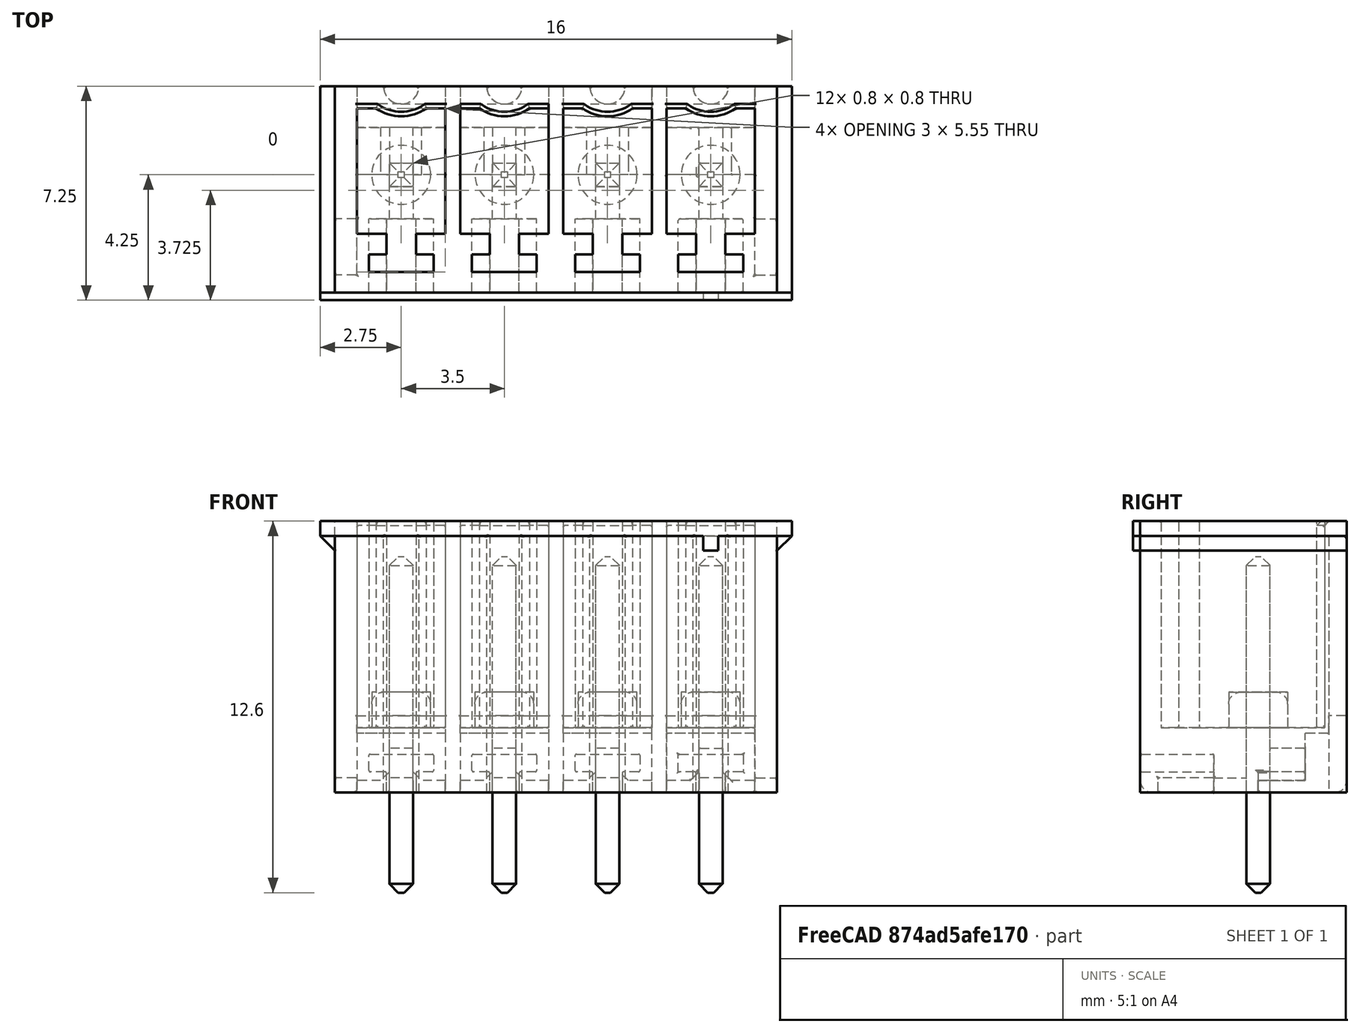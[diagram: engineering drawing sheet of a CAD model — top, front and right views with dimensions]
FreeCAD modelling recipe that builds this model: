
FCSTD DOCUMENT  (FreeCAD 0.15R4671 (Git))
Label: 4PIN
License: All rights reserved
LicenseURL: http://en.wikipedia.org/wiki/All_rights_reserved
objects: PartDesign::Fillet×102, PartDesign::Chamfer×18, Sketcher::SketchObject×15, PartDesign::Pocket×9, PartDesign::LinearPattern×9, PartDesign::Pad×6, PartDesign::Mirrored×2, Image::ImagePlane×1, Part::Cut×1
note: 177 computed .brp shape members not serialized (recipe doc carries the construction recipe); baked Part::Feature solids carry a one-line shape summary decoded from their .brp

FEATURE [Sketcher::SketchObject] Sketch
  sketch-geometry (4):
    g0: LineSegment StartX=-7.5 StartY=3 StartZ=0 EndX=7.5 EndY=3 EndZ=0
    g1: LineSegment StartX=7.5 StartY=3 StartZ=0 EndX=7.5 EndY=-4 EndZ=0
    g2: LineSegment StartX=7.5 StartY=-4 StartZ=0 EndX=-7.5 EndY=-4 EndZ=0
    g3: LineSegment StartX=-7.5 StartY=-4 StartZ=0 EndX=-7.5 EndY=3 EndZ=0
  constraints (12):
    c: Coincident(g0,g1)
    c: Coincident(g1,g2)
    c: Coincident(g2,g3)
    c: Coincident(g3,g0)
    c: Horizontal(g0)
    c: Horizontal(g2)
    c: Vertical(g1)
    c: Vertical(g3)
    c: DistanceX(g0) = 15
    c: DistanceY(g1) = -7
    c: Symmetric(g0,g0,g-2)
    c: DistanceY(g-1,g2) = -4
FEATURE [PartDesign::Pad] Pad
  Length = 9.2
  Length2 = 100
  Sketch = -> Sketch
  Type = 0
FEATURE [Sketcher::SketchObject] Sketch001
  Placement = pos=(0,0,-3.4) rot=(0,0,1;0rad)
  sketch-geometry (16):
    g0: LineSegment StartX=-5.65 StartY=0.4 StartZ=0 EndX=-4.85 EndY=0.4 EndZ=0
    g1: LineSegment StartX=-4.85 StartY=0.4 StartZ=0 EndX=-4.85 EndY=-0.4 EndZ=0
    g2: LineSegment StartX=-4.85 StartY=-0.4 StartZ=0 EndX=-5.65 EndY=-0.4 EndZ=0
    g3: LineSegment StartX=-5.65 StartY=-0.4 StartZ=0 EndX=-5.65 EndY=0.4 EndZ=0
    g4: LineSegment StartX=-2.15 StartY=0.4 StartZ=0 EndX=-1.35 EndY=0.4 EndZ=0
    g5: LineSegment StartX=-1.35 StartY=0.4 StartZ=0 EndX=-1.35 EndY=-0.4 EndZ=0
    g6: LineSegment StartX=-1.35 StartY=-0.4 StartZ=0 EndX=-2.15 EndY=-0.4 EndZ=0
    g7: LineSegment StartX=-2.15 StartY=-0.4 StartZ=0 EndX=-2.15 EndY=0.4 EndZ=0
    g8: LineSegment StartX=1.35 StartY=0.4 StartZ=0 EndX=2.15 EndY=0.4 EndZ=0
    g9: LineSegment StartX=2.15 StartY=0.4 StartZ=0 EndX=2.15 EndY=-0.4 EndZ=0
    g10: LineSegment StartX=2.15 StartY=-0.4 StartZ=0 EndX=1.35 EndY=-0.4 EndZ=0
    g11: LineSegment StartX=1.35 StartY=-0.4 StartZ=0 EndX=1.35 EndY=0.4 EndZ=0
    g12: LineSegment StartX=4.85 StartY=0.4 StartZ=0 EndX=5.65 EndY=0.4 EndZ=0
    g13: LineSegment StartX=5.65 StartY=0.4 StartZ=0 EndX=5.65 EndY=-0.4 EndZ=0
    g14: LineSegment StartX=5.65 StartY=-0.4 StartZ=0 EndX=4.85 EndY=-0.4 EndZ=0
    g15: LineSegment StartX=4.85 StartY=-0.4 StartZ=0 EndX=4.85 EndY=0.4 EndZ=0
  constraints (48):
    c: Coincident(g0,g1)
    c: Coincident(g1,g2)
    c: Coincident(g2,g3)
    c: Coincident(g3,g0)
    c: Horizontal(g0)
    c: Horizontal(g2)
    c: Vertical(g1)
    c: Vertical(g3)
    c: Coincident(g4,g5)
    c: Coincident(g5,g6)
    c: Coincident(g6,g7)
    c: Coincident(g7,g4)
    c: Horizontal(g4)
    c: Horizontal(g6)
    c: Vertical(g5)
    c: Vertical(g7)
    c: Coincident(g8,g9)
    c: Coincident(g9,g10)
    c: Coincident(g10,g11)
    c: Coincident(g11,g8)
    c: Horizontal(g8)
    c: Horizontal(g10)
    c: Vertical(g9)
    c: Vertical(g11)
    c: Coincident(g12,g13)
    c: Coincident(g13,g14)
    c: Coincident(g14,g15)
    c: Coincident(g15,g12)
    c: Horizontal(g12)
    c: Horizontal(g14)
    c: Vertical(g13)
    c: Vertical(g15)
    c: Equal(g0,g1)
    c: Equal(g1,g4)
    c: Equal(g4,g5)
    c: Equal(g5,g8)
    c: Equal(g8,g9)
    c: Equal(g9,g12)
    c: Equal(g12,g13)
    c: DistanceX(g0) = 0.8
    c: Symmetric(g1,g0,g-1)
    c: Symmetric(g4,g5,g-1)
    c: Symmetric(g8,g10,g-1)
    c: Symmetric(g12,g14,g-1)
    c: Symmetric(g4,g8,g-2)
    c: DistanceX(g-1,g5) = -1.35
    c: DistanceX(g5,g1) = -3.5
    c: DistanceX(g10,g14) = 3.5
FEATURE [PartDesign::Pad] Pad001
  Length = 11.4
  Length2 = 100
  Placement = pos=(0,0,-3.4) rot=(0,0,1;0rad)
  Sketch = -> Sketch001
  Type = 0
FEATURE [Sketcher::SketchObject] Sketch002
  Placement = pos=(0,0,9.2) rot=(0,0,1;0rad)
  Support = -> Pad [Face6]
  sketch-geometry (14):
    g0: LineSegment StartX=-6.1 StartY=2.25 StartZ=0 EndX=-6.75 EndY=2.25 EndZ=0
    g1: LineSegment StartX=-6.75 StartY=2.25 StartZ=0 EndX=-6.75 EndY=-2 EndZ=0
    g2: LineSegment StartX=-6.75 StartY=-2 StartZ=0 EndX=-5.75 EndY=-2 EndZ=0
    g3: LineSegment StartX=-5.75 StartY=-2 StartZ=0 EndX=-5.75 EndY=-2.7 EndZ=0
    g4: LineSegment StartX=-5.75 StartY=-2.7 StartZ=0 EndX=-6.35 EndY=-2.7 EndZ=0
    g5: LineSegment StartX=-6.35 StartY=-2.7 StartZ=0 EndX=-6.35 EndY=-3.3 EndZ=0
    g6: LineSegment StartX=-6.35 StartY=-3.3 StartZ=0 EndX=-4.15 EndY=-3.3 EndZ=0
    g7: LineSegment StartX=-4.15 StartY=-3.3 StartZ=0 EndX=-4.15 EndY=-2.7 EndZ=0
    g8: LineSegment StartX=-4.15 StartY=-2.7 StartZ=0 EndX=-4.75 EndY=-2.7 EndZ=0
    g9: LineSegment StartX=-4.75 StartY=-2.7 StartZ=0 EndX=-4.75 EndY=-2 EndZ=0
    g10: LineSegment StartX=-4.75 StartY=-2 StartZ=0 EndX=-3.75 EndY=-2 EndZ=0
    g11: LineSegment StartX=-3.75 StartY=-2 StartZ=0 EndX=-3.75 EndY=2.25 EndZ=0
    g12: LineSegment StartX=-3.75 StartY=2.25 StartZ=0 EndX=-4.4 EndY=2.25 EndZ=0
    g13: ArcOfCircle CenterX=-5.25 CenterY=3.48592 CenterZ=0 NormalX=0 NormalY=0 NormalZ=1 Radius=1.5 StartAngle=4.10993 EndAngle=5.31484
  constraints (43):
    c: Horizontal(g0)
    c: Coincident(g0,g1)
    c: Vertical(g1)
    c: Coincident(g1,g2)
    c: Horizontal(g2)
    c: Coincident(g2,g3)
    c: Vertical(g3)
    c: Coincident(g3,g4)
    c: Horizontal(g4)
    c: Coincident(g4,g5)
    c: Vertical(g5)
    c: Coincident(g5,g6)
    c: Horizontal(g6)
    c: Coincident(g6,g7)
    c: Vertical(g7)
    c: Coincident(g7,g8)
    c: Horizontal(g8)
    c: Coincident(g8,g9)
    c: Vertical(g9)
    c: Coincident(g9,g10)
    c: Horizontal(g10)
    c: Coincident(g10,g11)
    c: Vertical(g11)
    c: Coincident(g11,g12)
    c: Horizontal(g12)
    c: Equal(g1,g11)
    c: Equal(g0,g12)
    c: Equal(g2,g10)
    c: Equal(g3,g9)
    c: Equal(g4,g8)
    c: Equal(g5,g7)
    c: DistanceY(g1) = -4.25
    c: DistanceY(g3) = -0.7
    c: DistanceY(g7) = 0.6
    c: DistanceY(g-1,g9) = -2
    c: Coincident(g13,g0)
    c: Coincident(g13,g12)
    c: Radius(g13) = 1.5
    c: DistanceX(g0,g11) = 3
    c: DistanceX(g0) = -0.65
    c: DistanceX(g3,g8) = 1
    c: DistanceX(g6) = 2.2
    c: DistanceX(g-1,g13) = -5.25
FEATURE [Image::ImagePlane] ImagePlane
  Placement = pos=(0,-0.6,9.2) rot=(0,0,1;0rad)
  XSize = 11.5
  YSize = 7.25
FEATURE [PartDesign::Pocket] Pocket
  Length = 7
  Sketch = -> Sketch002
  Type = 0
FEATURE [PartDesign::LinearPattern] LinearPattern
  Direction = -> Sketch002 [H_Axis]
  Length = 10.5
  Occurrences = 4
  Originals = -> [Pocket]
FEATURE [Sketcher::SketchObject] Sketch003
  Placement = pos=(0,0,2.2) rot=(0,0,1;0rad)
  Support = -> LinearPattern [Face65]
  sketch-geometry (1):
    g0: Circle CenterX=-5.25 CenterY=0 CenterZ=0 NormalX=0 NormalY=0 NormalZ=1 Radius=1
  constraints (3):
    c: PointOnObject(g0,g-1)
    c: Radius(g0) = 1
    c: DistanceX(g-1,g0) = -5.25
FEATURE [PartDesign::Pad] Pad002
  Length = 1.2
  Length2 = 100
  Sketch = -> Sketch003
  Type = 0
FEATURE [PartDesign::LinearPattern] LinearPattern001
  Direction = -> Sketch003 [H_Axis]
  Length = 10.5
  Occurrences = 4
  Originals = -> [Pad002]
FEATURE [Sketcher::SketchObject] Sketch004
  Placement = pos=(0,0,-3.4) rot=(0,0,1;0rad)
  sketch-geometry (16):
    g0: LineSegment StartX=-5.65 StartY=0.4 StartZ=0 EndX=-4.85 EndY=0.4 EndZ=0
    g1: LineSegment StartX=-4.85 StartY=0.4 StartZ=0 EndX=-4.85 EndY=-0.4 EndZ=0
    g2: LineSegment StartX=-4.85 StartY=-0.4 StartZ=0 EndX=-5.65 EndY=-0.4 EndZ=0
    g3: LineSegment StartX=-5.65 StartY=-0.4 StartZ=0 EndX=-5.65 EndY=0.4 EndZ=0
    g4: LineSegment StartX=-2.15 StartY=0.4 StartZ=0 EndX=-1.35 EndY=0.4 EndZ=0
    g5: LineSegment StartX=-1.35 StartY=0.4 StartZ=0 EndX=-1.35 EndY=-0.4 EndZ=0
    g6: LineSegment StartX=-1.35 StartY=-0.4 StartZ=0 EndX=-2.15 EndY=-0.4 EndZ=0
    g7: LineSegment StartX=-2.15 StartY=-0.4 StartZ=0 EndX=-2.15 EndY=0.4 EndZ=0
    g8: LineSegment StartX=1.35 StartY=0.4 StartZ=0 EndX=2.15 EndY=0.4 EndZ=0
    g9: LineSegment StartX=2.15 StartY=0.4 StartZ=0 EndX=2.15 EndY=-0.4 EndZ=0
    g10: LineSegment StartX=2.15 StartY=-0.4 StartZ=0 EndX=1.35 EndY=-0.4 EndZ=0
    g11: LineSegment StartX=1.35 StartY=-0.4 StartZ=0 EndX=1.35 EndY=0.4 EndZ=0
    g12: LineSegment StartX=4.85 StartY=0.4 StartZ=0 EndX=5.65 EndY=0.4 EndZ=0
    g13: LineSegment StartX=5.65 StartY=0.4 StartZ=0 EndX=5.65 EndY=-0.4 EndZ=0
    g14: LineSegment StartX=5.65 StartY=-0.4 StartZ=0 EndX=4.85 EndY=-0.4 EndZ=0
    g15: LineSegment StartX=4.85 StartY=-0.4 StartZ=0 EndX=4.85 EndY=0.4 EndZ=0
  constraints (48):
    c: Coincident(g0,g1)
    c: Coincident(g1,g2)
    c: Coincident(g2,g3)
    c: Coincident(g3,g0)
    c: Horizontal(g0)
    c: Horizontal(g2)
    c: Vertical(g1)
    c: Vertical(g3)
    c: Coincident(g4,g5)
    c: Coincident(g5,g6)
    c: Coincident(g6,g7)
    c: Coincident(g7,g4)
    c: Horizontal(g4)
    c: Horizontal(g6)
    c: Vertical(g5)
    c: Vertical(g7)
    c: Coincident(g8,g9)
    c: Coincident(g9,g10)
    c: Coincident(g10,g11)
    c: Coincident(g11,g8)
    c: Horizontal(g8)
    c: Horizontal(g10)
    c: Vertical(g9)
    c: Vertical(g11)
    c: Coincident(g12,g13)
    c: Coincident(g13,g14)
    c: Coincident(g14,g15)
    c: Coincident(g15,g12)
    c: Horizontal(g12)
    c: Horizontal(g14)
    c: Vertical(g13)
    c: Vertical(g15)
    c: Equal(g0,g1)
    c: Equal(g1,g4)
    c: Equal(g4,g5)
    c: Equal(g5,g8)
    c: Equal(g8,g9)
    c: Equal(g9,g12)
    c: Equal(g12,g13)
    c: DistanceX(g0) = 0.8
    c: Symmetric(g1,g0,g-1)
    c: Symmetric(g4,g5,g-1)
    c: Symmetric(g8,g10,g-1)
    c: Symmetric(g12,g14,g-1)
    c: Symmetric(g4,g8,g-2)
    c: DistanceX(g-1,g5) = -1.35
    c: DistanceX(g5,g1) = -3.5
    c: DistanceX(g10,g14) = 3.5
FEATURE [PartDesign::Pad] Pad003
  Length = 10.2
  Length2 = 100
  Placement = pos=(0,0,-3.4) rot=(0,0,1;0rad)
  Sketch = -> Sketch004
  Type = 0
FEATURE [Part::Cut] Cut
  Base = -> LinearPattern001
  Tool = -> Pad003
FEATURE [Sketcher::SketchObject] Sketch005
  Placement = pos=(0,0,0) rot=(1,0,0;3.14159rad)
  Support = -> Cut [Face8]
  sketch-geometry (2):
    g0: LineSegment StartX=-5.85 StartY=-3 StartZ=0 EndX=-4.65 EndY=-3 EndZ=0
    g1: ArcOfCircle CenterX=-5.25 CenterY=-3 CenterZ=0 NormalX=0 NormalY=0 NormalZ=1 Radius=0.6 StartAngle=0 EndAngle=3.14159
  constraints (7):
    c: Horizontal(g0)
    c: DistanceX(g0) = 1.2
    c: PointOnObject(g1,g0)
    c: Coincident(g1,g0)
    c: Coincident(g1,g0)
    c: DistanceX(g-1,g1) = -5.25
    c: DistanceY(g-1,g1) = -3
FEATURE [PartDesign::Pocket] Pocket001
  Length = 8.7
  Sketch = -> Sketch005
  Type = 0
FEATURE [PartDesign::LinearPattern] LinearPattern002
  Direction = -> Sketch005 [H_Axis]
  Length = 10.5
  Occurrences = 4
  Originals = -> [Pocket001]
FEATURE [Sketcher::SketchObject] Sketch006
  ExternalGeometry = -> [LinearPattern002]
  Placement = pos=(0,-4,0) rot=(1,0,0;1.5708rad)
  Support = -> LinearPattern002 [Face29]
  sketch-geometry (4):
    g0: LineSegment StartX=-7.5 StartY=9.2 StartZ=0 EndX=-8 EndY=9.2 EndZ=0
    g1: LineSegment StartX=-8 StartY=9.2 StartZ=0 EndX=-8 EndY=8.7 EndZ=0
    g2: LineSegment StartX=-8 StartY=8.7 StartZ=0 EndX=-7.5 EndY=8.2 EndZ=0
    g3: LineSegment StartX=-7.5 StartY=8.2 StartZ=0 EndX=-7.5 EndY=9.2 EndZ=0
  constraints (11):
    c: Horizontal(g0)
    c: Coincident(g0,g1)
    c: Vertical(g1)
    c: Coincident(g1,g2)
    c: Coincident(g2,g3)
    c: Coincident(g3,g0)
    c: Vertical(g3)
    c: Coincident(g0,g-3)
    c: DistanceX(g0) = -0.5
    c: DistanceY(g1) = -0.5
    c: Angle(g-3,g2) = 0.785398
FEATURE [PartDesign::Pad] Pad004
  Length = 7
  Length2 = 100
  Reversed = true
  Sketch = -> Sketch006
  Type = 0
FEATURE [PartDesign::Mirrored] Mirrored
  MirrorPlane = -> Sketch006 [V_Axis]
  Originals = -> [Pad004]
FEATURE [Sketcher::SketchObject] Sketch007
  ExternalGeometry = -> [Mirrored]
  Placement = pos=(0,-4,0) rot=(1,0,0;1.5708rad)
  Support = -> Mirrored [Face101]
  sketch-geometry (8):
    g0: LineSegment StartX=-8 StartY=9.2 StartZ=0 EndX=8 EndY=9.2 EndZ=0
    g1: LineSegment StartX=8 StartY=9.2 StartZ=0 EndX=8 EndY=8.7 EndZ=0
    g2: LineSegment StartX=8 StartY=8.7 StartZ=0 EndX=5.5 EndY=8.7 EndZ=0
    g3: LineSegment StartX=-8 StartY=8.7 StartZ=0 EndX=-8 EndY=9.2 EndZ=0
    g4: LineSegment StartX=5 StartY=8.7 StartZ=0 EndX=5 EndY=8.2 EndZ=0
    g5: LineSegment StartX=5 StartY=8.2 StartZ=0 EndX=5.5 EndY=8.2 EndZ=0
    g6: LineSegment StartX=5.5 StartY=8.2 StartZ=0 EndX=5.5 EndY=8.7 EndZ=0
    g7: LineSegment StartX=5 StartY=8.7 StartZ=0 EndX=-8 EndY=8.7 EndZ=0
  constraints (25):
    c: Coincident(g0,g1)
    c: Coincident(g1,g2)
    c: Coincident(g7,g3)
    c: Coincident(g3,g0)
    c: Horizontal(g0)
    c: Horizontal(g2)
    c: Vertical(g1)
    c: Vertical(g3)
    c: PointOnObject(g0,g-3)
    c: DistanceY(g3) = 0.5
    c: PointOnObject(g0,g-4)
    c: Symmetric(g0,g0,g-2)
    c: Coincident(g4,g5)
    c: Coincident(g5,g6)
    c: Horizontal(g5)
    c: Vertical(g4)
    c: Vertical(g6)
    c: PointOnObject(g6,g2)
    c: DistanceY(g4,g-5) = 0
    c: Equal(g5,g4)
    c: DistanceX(g-1,g4) = 5
    c: PointOnObject(g2,g6)
    c: PointOnObject(g7,g4)
    c: Tangent(g2,g7)
    c: DistanceX(g2) = -2.5
FEATURE [PartDesign::Pad] Pad005
  Length = 0.25
  Length2 = 100
  Sketch = -> Sketch007
  Type = 0
FEATURE [Sketcher::SketchObject] Sketch008
  Placement = pos=(0,-4,0) rot=(1,0,0;1.5708rad)
  Support = -> Pad005 [Face66]
  sketch-geometry (8):
    g0: LineSegment StartX=-5.75 StartY=0 StartZ=0 EndX=-5.75 EndY=0.7 EndZ=0
    g1: LineSegment StartX=-5.75 StartY=0.7 StartZ=0 EndX=-6.35 EndY=0.7 EndZ=0
    g2: LineSegment StartX=-6.35 StartY=0.7 StartZ=0 EndX=-6.35 EndY=1.3 EndZ=0
    g3: LineSegment StartX=-6.35 StartY=1.3 StartZ=0 EndX=-4.15 EndY=1.3 EndZ=0
    g4: LineSegment StartX=-4.15 StartY=1.3 StartZ=0 EndX=-4.15 EndY=0.7 EndZ=0
    g5: LineSegment StartX=-4.15 StartY=0.7 StartZ=0 EndX=-4.75 EndY=0.7 EndZ=0
    g6: LineSegment StartX=-4.75 StartY=0.7 StartZ=0 EndX=-4.75 EndY=0 EndZ=0
    g7: LineSegment StartX=-4.75 StartY=0 StartZ=0 EndX=-5.75 EndY=0 EndZ=0
  constraints (25):
    c: Vertical(g0)
    c: Coincident(g0,g1)
    c: Horizontal(g1)
    c: Coincident(g1,g2)
    c: Coincident(g2,g3)
    c: Horizontal(g3)
    c: Coincident(g3,g4)
    c: Coincident(g4,g5)
    c: Horizontal(g5)
    c: Coincident(g5,g6)
    c: Vertical(g6)
    c: Coincident(g6,g7)
    c: Horizontal(g7)
    c: Coincident(g0,g7)
    c: Vertical(g4)
    c: Equal(g5,g1)
    c: Vertical(g2)
    c: Equal(g4,g2)
    c: Equal(g0,g6)
    c: DistanceX(g3) = 2.2
    c: DistanceX(g7) = -1
    c: DistanceY(g4) = -0.6
    c: DistanceY(g-1,g4) = 0.7
    c: DistanceX(g-1,g6) = -4.75
    c: PointOnObject(g6,g-1)
FEATURE [PartDesign::Pocket] Pocket002
  Length = 2.5
  Sketch = -> Sketch008
  Type = 0
FEATURE [PartDesign::LinearPattern] LinearPattern003
  Direction = -> Sketch008 [H_Axis]
  Length = 10.5
  Occurrences = 4
  Originals = -> [Pocket002]
FEATURE [Sketcher::SketchObject] Sketch009
  Placement = pos=(0,3,0) rot=(0,0.707107,0.707107;3.14159rad)
  Support = -> LinearPattern003 [Face10]
  sketch-geometry (4):
    g0: LineSegment StartX=-6.75 StartY=2 StartZ=0 EndX=-3.75 EndY=2 EndZ=0
    g1: LineSegment StartX=-3.75 StartY=2 StartZ=0 EndX=-3.75 EndY=0 EndZ=0
    g2: LineSegment StartX=-3.75 StartY=0 StartZ=0 EndX=-6.75 EndY=0 EndZ=0
    g3: LineSegment StartX=-6.75 StartY=0 StartZ=0 EndX=-6.75 EndY=2 EndZ=0
  constraints (12):
    c: Coincident(g0,g1)
    c: Coincident(g1,g2)
    c: Coincident(g2,g3)
    c: Coincident(g3,g0)
    c: Horizontal(g0)
    c: Horizontal(g2)
    c: Vertical(g1)
    c: Vertical(g3)
    c: PointOnObject(g1,g-1)
    c: DistanceX(g2) = -3
    c: DistanceY(g1) = -2
    c: DistanceX(g-1,g1) = -3.75
FEATURE [PartDesign::Pocket] Pocket003
  Length = 1.4
  Sketch = -> Sketch009
  Type = 0
FEATURE [PartDesign::LinearPattern] LinearPattern004
  Direction = -> Sketch009 [H_Axis]
  Length = 10.5
  Occurrences = 4
  Originals = -> [Pocket003]
FEATURE [Sketcher::SketchObject] Sketch010
  ExternalGeometry = -> [LinearPattern004]
  Placement = pos=(0,3,0) rot=(0,0.707107,0.707107;3.14159rad)
  Support = -> LinearPattern004 [Face10]
  sketch-geometry (4):
    g0: LineSegment StartX=-6.75 StartY=2 StartZ=0 EndX=-3.75 EndY=2 EndZ=0
    g1: LineSegment StartX=-3.75 StartY=2 StartZ=0 EndX=-3.75 EndY=2.6 EndZ=0
    g2: LineSegment StartX=-3.75 StartY=2.6 StartZ=0 EndX=-6.75 EndY=2.6 EndZ=0
    g3: LineSegment StartX=-6.75 StartY=2.6 StartZ=0 EndX=-6.75 EndY=2 EndZ=0
  constraints (11):
    c: Coincident(g0,g1)
    c: Coincident(g1,g2)
    c: Coincident(g2,g3)
    c: Coincident(g3,g0)
    c: Horizontal(g0)
    c: Horizontal(g2)
    c: Vertical(g1)
    c: Vertical(g3)
    c: Coincident(g0,g-3)
    c: DistanceX(g0) = 3
    c: DistanceY(g1) = 0.6
FEATURE [PartDesign::Pocket] Pocket004
  Length = 0.6
  Sketch = -> Sketch010
  Type = 0
FEATURE [PartDesign::LinearPattern] LinearPattern005
  Direction = -> Sketch010 [H_Axis]
  Length = 10.5
  Occurrences = 4
  Originals = -> [Pocket004]
FEATURE [Sketcher::SketchObject] Sketch011
  ExternalGeometry = -> [LinearPattern005]
  Placement = pos=(0,0,0) rot=(1,0,0;3.14159rad)
  Support = -> LinearPattern005 [Face72]
  sketch-geometry (4):
    g0: LineSegment StartX=-6.75 StartY=-1.6 StartZ=0 EndX=-3.75 EndY=-1.6 EndZ=0
    g1: LineSegment StartX=-3.75 StartY=-1.6 StartZ=0 EndX=-3.75 EndY=0 EndZ=0
    g2: LineSegment StartX=-3.75 StartY=0 StartZ=0 EndX=-6.75 EndY=0 EndZ=0
    g3: LineSegment StartX=-6.75 StartY=0 StartZ=0 EndX=-6.75 EndY=-1.6 EndZ=0
  constraints (11):
    c: Coincident(g0,g1)
    c: Coincident(g1,g2)
    c: Coincident(g2,g3)
    c: Coincident(g3,g0)
    c: Horizontal(g0)
    c: Horizontal(g2)
    c: Vertical(g1)
    c: Vertical(g3)
    c: Coincident(g0,g-4)
    c: PointOnObject(g1,g-1)
    c: Coincident(g0,g-4)
FEATURE [PartDesign::Pocket] Pocket005
  Length = 0.4
  Sketch = -> Sketch011
  Type = 0
FEATURE [PartDesign::LinearPattern] LinearPattern006
  Direction = -> Sketch011 [H_Axis]
  Length = 10.5
  Occurrences = 4
  Originals = -> [Pocket005]
FEATURE [Sketcher::SketchObject] Sketch012
  ExternalGeometry = -> [LinearPattern006]
  Placement = pos=(0,0,0) rot=(1,0,0;3.14159rad)
  Support = -> LinearPattern006 [Face72]
  sketch-geometry (4):
    g0: LineSegment StartX=-5.65 StartY=0.4 StartZ=0 EndX=-4.85 EndY=0.4 EndZ=0
    g1: LineSegment StartX=-4.85 StartY=0.4 StartZ=0 EndX=-4.85 EndY=1.5 EndZ=0
    g2: LineSegment StartX=-4.85 StartY=1.5 StartZ=0 EndX=-5.65 EndY=1.5 EndZ=0
    g3: LineSegment StartX=-5.65 StartY=1.5 StartZ=0 EndX=-5.65 EndY=0.4 EndZ=0
  constraints (11):
    c: Coincident(g0,g1)
    c: Coincident(g1,g2)
    c: Coincident(g2,g3)
    c: Coincident(g3,g0)
    c: Horizontal(g0)
    c: Horizontal(g2)
    c: Vertical(g1)
    c: Vertical(g3)
    c: Coincident(g0,g-4)
    c: PointOnObject(g2,g-5)
    c: Coincident(g0,g-3)
FEATURE [PartDesign::Pocket] Pocket006
  Length = 0.5
  Sketch = -> Sketch012
  Type = 0
FEATURE [PartDesign::LinearPattern] LinearPattern007
  Direction = -> Sketch012 [H_Axis]
  Length = 10.5
  Occurrences = 4
  Originals = -> [Pocket006]
FEATURE [Sketcher::SketchObject] Sketch013
  ExternalGeometry = -> [LinearPattern007]
  Placement = pos=(0,0,0.4) rot=(1,0,0;3.14159rad)
  Support = -> LinearPattern007 [Face114]
  sketch-geometry (4):
    g0: LineSegment StartX=-5.65 StartY=-0.4 StartZ=0 EndX=-4.85 EndY=-0.4 EndZ=0
    g1: LineSegment StartX=-4.85 StartY=-0.4 StartZ=0 EndX=-4.85 EndY=-1.6 EndZ=0
    g2: LineSegment StartX=-4.85 StartY=-1.6 StartZ=0 EndX=-5.65 EndY=-1.6 EndZ=0
    g3: LineSegment StartX=-5.65 StartY=-1.6 StartZ=0 EndX=-5.65 EndY=-0.4 EndZ=0
  constraints (11):
    c: Coincident(g0,g1)
    c: Coincident(g1,g2)
    c: Coincident(g2,g3)
    c: Coincident(g3,g0)
    c: Horizontal(g0)
    c: Horizontal(g2)
    c: Vertical(g1)
    c: Vertical(g3)
    c: Coincident(g0,g-3)
    c: PointOnObject(g1,g-4)
    c: Coincident(g0,g-3)
FEATURE [PartDesign::Pocket] Pocket007
  Length = 1.1
  Sketch = -> Sketch013
  Type = 0
FEATURE [PartDesign::LinearPattern] LinearPattern008
  Direction = -> Sketch013 [H_Axis]
  Length = 10.5
  Occurrences = 4
  Originals = -> [Pocket007]
FEATURE [Sketcher::SketchObject] Sketch014
  ExternalGeometry = -> [LinearPattern008]
  Placement = pos=(0,0,0) rot=(1,0,0;3.14159rad)
  Support = -> LinearPattern008 [Face72]
  sketch-geometry (4):
    g0: LineSegment StartX=-7.5 StartY=3.4 StartZ=0 EndX=-6.75 EndY=3.4 EndZ=0
    g1: LineSegment StartX=-6.75 StartY=3.4 StartZ=0 EndX=-6.75 EndY=1.5 EndZ=0
    g2: LineSegment StartX=-6.75 StartY=1.5 StartZ=0 EndX=-7.5 EndY=1.5 EndZ=0
    g3: LineSegment StartX=-7.5 StartY=1.5 StartZ=0 EndX=-7.5 EndY=3.4 EndZ=0
  constraints (12):
    c: Coincident(g0,g1)
    c: Coincident(g1,g2)
    c: Coincident(g2,g3)
    c: Coincident(g3,g0)
    c: Horizontal(g0)
    c: Horizontal(g2)
    c: Vertical(g1)
    c: Vertical(g3)
    c: PointOnObject(g0,g-4)
    c: PointOnObject(g1,g-3)
    c: DistanceY(g0,g-4) = 0.6
    c: PointOnObject(g1,g-5)
FEATURE [PartDesign::Pocket] Pocket008
  Length = 0.5
  Sketch = -> Sketch014
  Type = 0
FEATURE [PartDesign::Mirrored] Mirrored001
  MirrorPlane = -> Sketch014 [V_Axis]
  Originals = -> [Pocket008]
FEATURE [PartDesign::Chamfer] Chamfer
  Base = -> Pad001 [Edge21,Edge23,Edge18,Edge15]
  Placement = pos=(0,0,-3.4) rot=(0,0,1;0rad)
  Size = 0.3
FEATURE [PartDesign::Chamfer] Chamfer001
  Base = -> Chamfer [Edge3,Edge7,Edge11,Edge12]
  Placement = pos=(0,0,-3.4) rot=(0,0,1;0rad)
  Size = 0.3
FEATURE [PartDesign::Fillet] Fillet
  Base = -> Chamfer001 [Edge16,Edge5,Edge4,Edge1]
  Placement = pos=(0,0,-3.4) rot=(0,0,1;0rad)
  Radius = 0.05
FEATURE [PartDesign::Chamfer] Chamfer002
  Base = -> Fillet [Edge83,Edge75,Edge81,Edge78,Edge76,Edge82,Edge79,Edge84]
  Placement = pos=(0,0,-3.4) rot=(0,0,1;0rad)
  Size = 0.3
FEATURE [PartDesign::Fillet] Fillet001
  Base = -> Chamfer002 [Edge1,Edge5,Edge4,Edge16]
  Placement = pos=(0,0,-3.4) rot=(0,0,1;0rad)
  Radius = 0.05
FEATURE [PartDesign::Chamfer] Chamfer003
  Base = -> Fillet001 [Edge111,Edge114,Edge117,Edge119,Edge120,Edge118,Edge115,Edge112]
  Placement = pos=(0,0,-3.4) rot=(0,0,1;0rad)
  Size = 0.3
FEATURE [PartDesign::Fillet] Fillet002
  Base = -> Chamfer003 [Edge1,Edge4,Edge16,Edge5]
  Placement = pos=(0,0,-3.4) rot=(0,0,1;0rad)
  Radius = 0.05
FEATURE [PartDesign::Chamfer] Chamfer004
  Base = -> Fillet002 [Edge147,Edge150,Edge155,Edge153,Edge154,Edge151,Edge148,Edge156]
  Placement = pos=(0,0,-3.4) rot=(0,0,1;0rad)
  Size = 0.3
FEATURE [PartDesign::Fillet] Fillet003  label="PINS"
  Base = -> Chamfer004 [Edge5,Edge16,Edge1,Edge4]
  Placement = pos=(0,0,-3.4) rot=(0,0,1;0rad)
  Radius = 0.05
FEATURE [PartDesign::Chamfer] Chamfer005
  Base = -> Mirrored001 [Edge65,Edge67]
  Size = 0.15
FEATURE [PartDesign::Chamfer] Chamfer006
  Base = -> Chamfer005 [Edge2]
  Size = 0.15
FEATURE [PartDesign::Fillet] Fillet004
  Base = -> Chamfer006 [Edge75,Edge89,Edge77,Edge91]
  Radius = 0.05
FEATURE [PartDesign::Fillet] Fillet005
  Base = -> Fillet004 [Edge80,Edge86,Edge106,Edge104,Edge88,Edge98,Edge91,Edge95]
  Radius = 0.05
FEATURE [PartDesign::Fillet] Fillet006
  Base = -> Fillet005 [Edge284]
  Radius = 0.05
FEATURE [PartDesign::Fillet] Fillet007
  Base = -> Fillet006 [Edge89]
  Radius = 0.4
FEATURE [PartDesign::Fillet] Fillet008
  Base = -> Fillet007 [Edge16]
  Radius = 0.05
FEATURE [PartDesign::Fillet] Fillet009
  Base = -> Fillet008 [Edge1]
  Radius = 0.05
FEATURE [PartDesign::Fillet] Fillet010
  Base = -> Fillet009 [Edge89]
  Radius = 0.05
FEATURE [PartDesign::Chamfer] Chamfer007
  Base = -> Fillet010 [Edge102,Edge100]
  Size = 0.15
FEATURE [PartDesign::Chamfer] Chamfer008
  Base = -> Chamfer007 [Edge7]
  Size = 0.15
FEATURE [PartDesign::Fillet] Fillet011
  Base = -> Chamfer008 [Edge91,Edge89,Edge103,Edge105]
  Radius = 0.05
FEATURE [PartDesign::Fillet] Fillet012
  Base = -> Fillet011 [Edge120,Edge94,Edge100,Edge118,Edge112,Edge102,Edge105,Edge109]
  Radius = 0.05
FEATURE [PartDesign::Fillet] Fillet013
  Base = -> Fillet012 [Edge332]
  Radius = 0.05
FEATURE [PartDesign::Fillet] Fillet014
  Base = -> Fillet013 [Edge89]
  Radius = 0.4
FEATURE [PartDesign::Fillet] Fillet015
  Base = -> Fillet014 [Edge16]
  Radius = 0.05
FEATURE [PartDesign::Fillet] Fillet016
  Base = -> Fillet015 [Edge83]
  Radius = 0.05
FEATURE [PartDesign::Chamfer] Chamfer009
  Base = -> Fillet016 [Edge111,Edge113]
  Size = 0.15
FEATURE [PartDesign::Chamfer] Chamfer010
  Base = -> Chamfer009 [Edge2]
  Size = 0.15
FEATURE [PartDesign::Fillet] Fillet017
  Base = -> Chamfer010 [Edge103,Edge105,Edge119,Edge117]
  Radius = 0.05
FEATURE [PartDesign::Fillet] Fillet018
  Base = -> Fillet017 [Edge108,Edge134,Edge114,Edge119,Edge116,Edge132,Edge126,Edge123]
  Radius = 0.05
FEATURE [PartDesign::Fillet] Fillet019
  Base = -> Fillet018 [Edge374]
  Radius = 0.05
FEATURE [PartDesign::Fillet] Fillet020
  Base = -> Fillet019 [Edge89]
  Radius = 0.4
FEATURE [PartDesign::Fillet] Fillet021
  Base = -> Fillet020 [Edge734]
  Radius = 0.05
FEATURE [PartDesign::Fillet] Fillet022
  Base = -> Fillet021 [Edge155]
  Radius = 0.05
FEATURE [PartDesign::Fillet] Fillet023
  Base = -> Fillet022 [Edge125]
  Radius = 0.05
FEATURE [PartDesign::Chamfer] Chamfer011
  Base = -> Fillet023 [Edge237,Edge235]
  Size = 0.15
FEATURE [PartDesign::Chamfer] Chamfer012
  Base = -> Chamfer011 [Edge7]
  Size = 0.15
FEATURE [PartDesign::Fillet] Fillet024
  Base = -> Chamfer012 [Edge119,Edge133,Edge135,Edge121]
  Radius = 0.05
FEATURE [PartDesign::Fillet] Fillet025
  Base = -> Fillet024 [Edge132,Edge130,Edge148,Edge124,Edge150,Edge139,Edge142,Edge135]
  Radius = 0.05
FEATURE [PartDesign::Fillet] Fillet026
  Base = -> Fillet025 [Edge134]
  Radius = 0.05
FEATURE [PartDesign::Fillet] Fillet027
  Base = -> Fillet026 [Edge141]
  Radius = 0.05
FEATURE [PartDesign::Fillet] Fillet028
  Base = -> Fillet027 [Edge21]
  Radius = 0.05
FEATURE [PartDesign::Fillet] Fillet029
  Base = -> Fillet028 [Edge75]
  Radius = 0.4
FEATURE [PartDesign::Fillet] Fillet030
  Base = -> Fillet029 [Edge167]
  Radius = 0.05
FEATURE [PartDesign::Chamfer] Chamfer013
  Base = -> Fillet030 [Edge1082]
  Size = 0.3
FEATURE [PartDesign::Chamfer] Chamfer014
  Base = -> Chamfer013 [Edge177]
  Size = 0.3
FEATURE [PartDesign::Chamfer] Chamfer015
  Base = -> Chamfer014 [Edge159,Edge466]
  Size = 0.3
FEATURE [PartDesign::Chamfer] Chamfer016
  Base = -> Chamfer015 [Edge769,Edge789]
  Size = 0.3
FEATURE [PartDesign::Chamfer] Chamfer017
  Base = -> Chamfer016 [Edge808,Edge828]
  Size = 0.3
FEATURE [PartDesign::Fillet] Fillet031
  Base = -> Chamfer017 [Edge342,Edge378]
  Radius = 0.1
FEATURE [PartDesign::Fillet] Fillet032
  Base = -> Fillet031 [Edge305,Edge326]
  Radius = 0.1
FEATURE [PartDesign::Fillet] Fillet033
  Base = -> Fillet032 [Edge340,Edge361]
  Radius = 0.1
FEATURE [PartDesign::Fillet] Fillet034
  Base = -> Fillet033 [Edge369,Edge399]
  Radius = 0.1
FEATURE [PartDesign::Fillet] Fillet035
  Base = -> Fillet034 [Edge84,Edge92,Edge100,Edge8,Edge114]
  Radius = 0.4
FEATURE [PartDesign::Fillet] Fillet036
  Base = -> Fillet035 [Edge97,Edge13,Edge82,Edge72,Edge62]
  Radius = 0.4
FEATURE [PartDesign::Fillet] Fillet037
  Base = -> Fillet036 [Edge61,Edge169,Edge77,Edge185]
  Radius = 0.05
FEATURE [PartDesign::Fillet] Fillet038
  Base = -> Fillet037 [Edge76,Edge199,Edge16,Edge8]
  Radius = 0.05
FEATURE [PartDesign::Fillet] Fillet039
  Base = -> Fillet038 [Edge65]
  Radius = 0.05
FEATURE [PartDesign::Fillet] Fillet040
  Base = -> Fillet039 [Edge519]
  Radius = 0.05
FEATURE [PartDesign::Fillet] Fillet041
  Base = -> Fillet040 [Edge66]
  Radius = 0.05
FEATURE [PartDesign::Fillet] Fillet042
  Base = -> Fillet041 [Edge48]
  Radius = 0.05
FEATURE [PartDesign::Fillet] Fillet043
  Base = -> Fillet042 [Edge55]
  Radius = 0.05
FEATURE [PartDesign::Fillet] Fillet044
  Base = -> Fillet043 [Edge11]
  Radius = 0.05
FEATURE [PartDesign::Fillet] Fillet045
  Base = -> Fillet044 [Edge174]
  Radius = 0.04
FEATURE [PartDesign::Fillet] Fillet046
  Base = -> Fillet045 [Edge31]
  Radius = 0.05
FEATURE [PartDesign::Fillet] Fillet047
  Base = -> Fillet046 [Edge175]
  Radius = 0.04
FEATURE [PartDesign::Fillet] Fillet048
  Base = -> Fillet047 [Edge715]
  Radius = 0.05
FEATURE [PartDesign::Fillet] Fillet049
  Base = -> Fillet048 [Edge4]
  Radius = 0.05
FEATURE [PartDesign::Fillet] Fillet050
  Base = -> Fillet049 [Edge127]
  Radius = 0.05
FEATURE [PartDesign::Fillet] Fillet051
  Base = -> Fillet050 [Edge4]
  Radius = 0.05
FEATURE [PartDesign::Fillet] Fillet052
  Base = -> Fillet051 [Edge133]
  Radius = 0.05
FEATURE [PartDesign::Fillet] Fillet053
  Base = -> Fillet052 [Edge4]
  Radius = 0.05
FEATURE [PartDesign::Fillet] Fillet054
  Base = -> Fillet053 [Edge135]
  Radius = 0.05
FEATURE [PartDesign::Fillet] Fillet055
  Base = -> Fillet054 [Edge4]
  Radius = 0.05
FEATURE [PartDesign::Fillet] Fillet056
  Base = -> Fillet055 [Edge52]
  Radius = 0.05
FEATURE [PartDesign::Fillet] Fillet057
  Base = -> Fillet056 [Edge24]
  Radius = 0.05
FEATURE [PartDesign::Fillet] Fillet058
  Base = -> Fillet057 [Edge275,Edge273]
  Radius = 0.05
FEATURE [PartDesign::Fillet] Fillet059
  Base = -> Fillet058 [Edge36]
  Radius = 0.05
FEATURE [PartDesign::Fillet] Fillet060
  Base = -> Fillet059 [Edge7]
  Radius = 0.05
FEATURE [PartDesign::Fillet] Fillet061
  Base = -> Fillet060 [Edge56,Edge50]
  Radius = 0.05
FEATURE [PartDesign::Fillet] Fillet062
  Base = -> Fillet061 [Edge1]
  Radius = 0.05
FEATURE [PartDesign::Fillet] Fillet063
  Base = -> Fillet062 [Edge1]
  Radius = 0.04
FEATURE [PartDesign::Fillet] Fillet064
  Base = -> Fillet063 [Edge114]
  Radius = 0.04
FEATURE [PartDesign::Fillet] Fillet065
  Base = -> Fillet064 [Edge211]
  Radius = 0.04
FEATURE [PartDesign::Fillet] Fillet066
  Base = -> Fillet065 [Edge107]
  Radius = 0.05
FEATURE [PartDesign::Fillet] Fillet067
  Base = -> Fillet066 [Edge4]
  Radius = 0.05
FEATURE [PartDesign::Fillet] Fillet068
  Base = -> Fillet067 [Edge286]
  Radius = 0.05
FEATURE [PartDesign::Fillet] Fillet069
  Base = -> Fillet068 [Edge179]
  Radius = 0.05
FEATURE [PartDesign::Fillet] Fillet070
  Base = -> Fillet069 [Edge117]
  Radius = 0.05
FEATURE [PartDesign::Fillet] Fillet071
  Base = -> Fillet070 [Edge75,Edge120,Edge133,Edge178]
  Radius = 0.05
FEATURE [PartDesign::Fillet] Fillet072
  Base = -> Fillet071 [Edge417,Edge418]
  Radius = 0.05
FEATURE [PartDesign::Fillet] Fillet073
  Base = -> Fillet072 [Edge63]
  Radius = 0.05
FEATURE [PartDesign::Fillet] Fillet074
  Base = -> Fillet073 [Edge57]
  Radius = 0.05
FEATURE [PartDesign::Fillet] Fillet075
  Base = -> Fillet074 [Edge80,Edge64]
  Radius = 0.05
FEATURE [PartDesign::Fillet] Fillet076
  Base = -> Fillet075 [Edge38]
  Radius = 0.05
FEATURE [PartDesign::Fillet] Fillet077
  Base = -> Fillet076 [Edge623,Edge624]
  Radius = 0.05
FEATURE [PartDesign::Fillet] Fillet078
  Base = -> Fillet077 [Edge6]
  Radius = 0.05
FEATURE [PartDesign::Fillet] Fillet079
  Base = -> Fillet078 [Edge57]
  Radius = 0.05
FEATURE [PartDesign::Fillet] Fillet080
  Base = -> Fillet079 [Edge77,Edge61]
  Radius = 0.05
FEATURE [PartDesign::Fillet] Fillet081
  Base = -> Fillet080 [Edge37]
  Radius = 0.05
FEATURE [PartDesign::Fillet] Fillet082
  Base = -> Fillet081 [Edge165]
  Radius = 0.05
FEATURE [PartDesign::Fillet] Fillet083
  Base = -> Fillet082 [Edge2]
  Radius = 0.05
FEATURE [PartDesign::Fillet] Fillet084
  Base = -> Fillet083 [Edge13]
  Radius = 0.05
FEATURE [PartDesign::Fillet] Fillet085
  Base = -> Fillet084 [Edge9]
  Radius = 0.05
FEATURE [PartDesign::Fillet] Fillet086
  Base = -> Fillet085 [Edge60]
  Radius = 0.05
FEATURE [PartDesign::Fillet] Fillet087
  Base = -> Fillet086 [Edge99]
  Radius = 0.05
FEATURE [PartDesign::Fillet] Fillet088
  Base = -> Fillet087 [Edge1]
  Radius = 0.049
FEATURE [PartDesign::Fillet] Fillet089
  Base = -> Fillet088 [Edge238,Edge215]
  Radius = 0.05
FEATURE [PartDesign::Fillet] Fillet090
  Base = -> Fillet089 [Edge10]
  Radius = 0.05
FEATURE [PartDesign::Fillet] Fillet091
  Base = -> Fillet090 [Edge370]
  Radius = 0.05
FEATURE [PartDesign::Fillet] Fillet092
  Base = -> Fillet091 [Edge68]
  Radius = 0.05
FEATURE [PartDesign::Fillet] Fillet093
  Base = -> Fillet092 [Edge69]
  Radius = 0.05
FEATURE [PartDesign::Fillet] Fillet094
  Base = -> Fillet093 [Edge81]
  Radius = 0.05
FEATURE [PartDesign::Fillet] Fillet095
  Base = -> Fillet094 [Edge71]
  Radius = 0.05
FEATURE [PartDesign::Fillet] Fillet096
  Base = -> Fillet095 [Edge102]
  Radius = 0.05
FEATURE [PartDesign::Fillet] Fillet097
  Base = -> Fillet096 [Edge9]
  Radius = 0.05
FEATURE [PartDesign::Fillet] Fillet098
  Base = -> Fillet097 [Edge80,Edge84,Edge88,Edge76,Edge70,Edge92]
  Radius = 0.05
FEATURE [PartDesign::Fillet] Fillet099
  Base = -> Fillet098 [Edge12]
  Radius = 0.05
FEATURE [PartDesign::Fillet] Fillet100
  Base = -> Fillet099 [Edge145,Edge151,Edge127,Edge133,Edge141,Edge137]
  Radius = 0.05
FEATURE [PartDesign::Fillet] Fillet101  label="HOUSING"
  Base = -> Fillet100 [Edge12]
  Radius = 0.05
